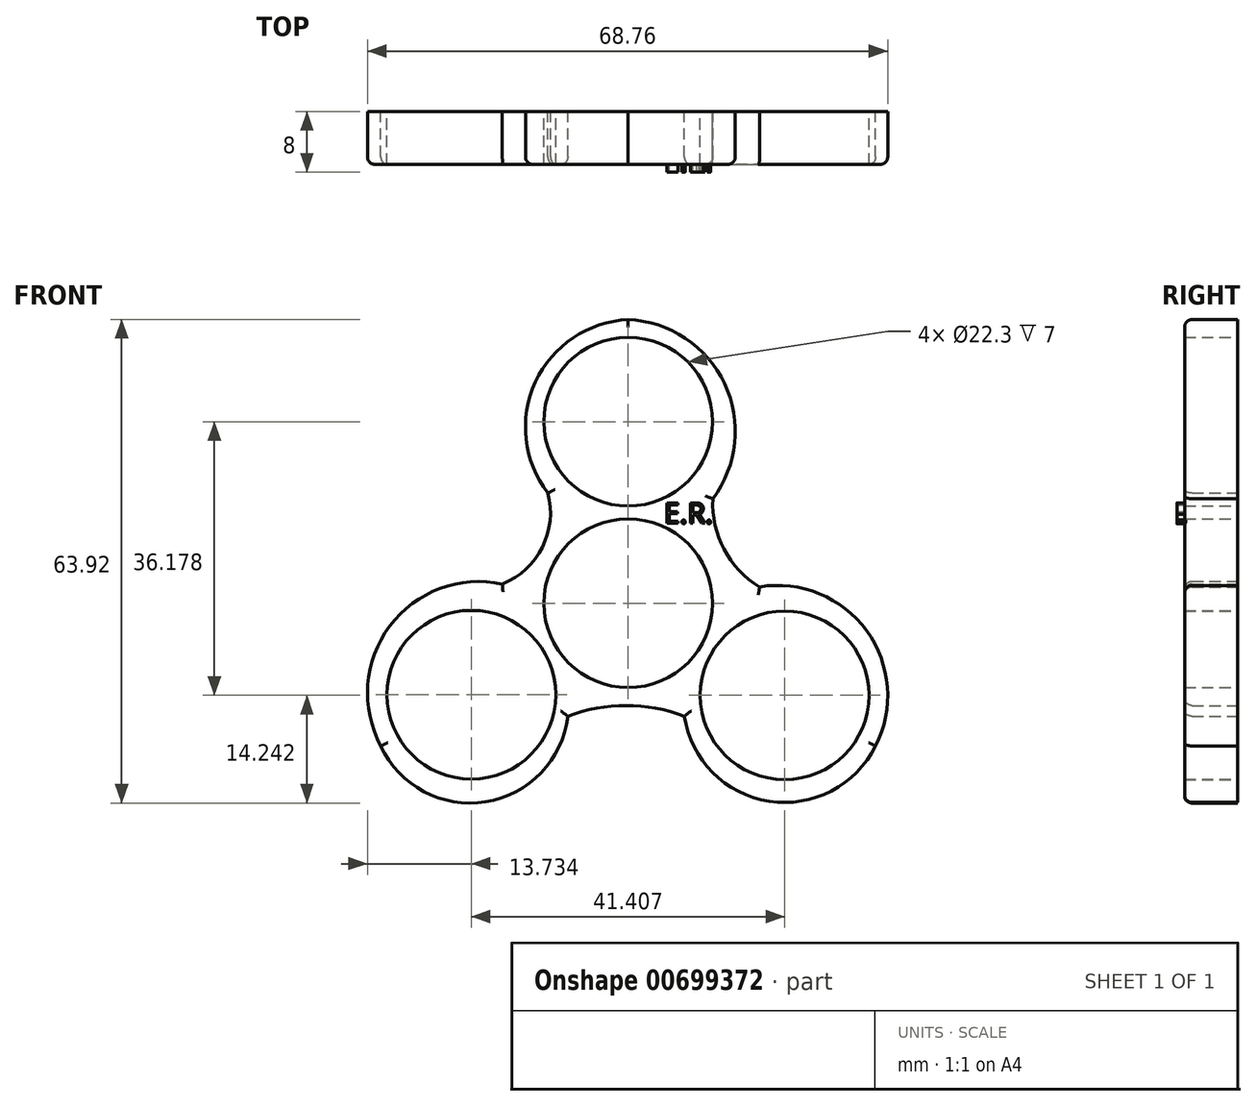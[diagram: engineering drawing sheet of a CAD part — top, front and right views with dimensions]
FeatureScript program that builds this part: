
annotation { "Feature Type Name" : "Feature", "Feature Type Description" : "" }
export const myFeature = defineFeature(function(context is Context, id is Id, definition is map)
    precondition{}
    {
        {
            var Q0;
            Q0=qCreatedBy(makeId("Front.planeOp"),FACE);
            var sketch = newSketch(context, id + "F0", { "sketchPlane" : qUnion([Q0])});
            skCircle(sketch, "E0", {"center": v(0, 0) * mm, "radius": 11.15 * mm});
            skCircle(sketch, "E1", {"center": v(0, 24) * mm, "radius": 11.15 * mm});
            skCircle(sketch, "E2", {"center": v(20.68, -12.18) * mm, "radius": 11.15 * mm});
            skCircle(sketch, "E3", {"center": v(-20.73, -12.1) * mm, "radius": 11.15 * mm});
            skLineSegment(sketch, "E4", {"start": v(0, 0) * mm, "end": v(-44.43, -25.65) * mm});
            skLineSegment(sketch, "E5", {"start": v(0, 0) * mm, "end": v(44.43, -25.65) * mm});
            skLineSegment(sketch, "E6", {"start": v(0, 0) * mm, "end": v(0, 54.97) * mm});
            skArc(sketch, "E7", {"start": v(-16.63, 2.54) * mm, "mid": v(-11.35, 7.41) * mm, "end": v(-10.62, 14.57) * mm});
            skArc(sketch, "E8", {"start": v(-16.63, 2.54) * mm, "mid": v(-31.51, -3.03) * mm, "end": v(-32.7, -18.88) * mm});
            skArc(sketch, "E9", {"start": v(-32.7, -18.88) * mm, "mid": v(-18.85, -26.26) * mm, "end": v(-7.99, -14.94) * mm});
            skArc(sketch, "E10", {"start": v(7.42, -14.94) * mm, "mid": v(-0.28, -13.53) * mm, "end": v(-7.99, -14.94) * mm});
            skArc(sketch, "E11", {"start": v(7.42, -14.94) * mm, "mid": v(18.62, -26.18) * mm, "end": v(32.7, -18.88) * mm});
            skArc(sketch, "E12", {"start": v(32.7, -18.88) * mm, "mid": v(31.51, -3.65) * mm, "end": v(17.39, 2.16) * mm});
            skArc(sketch, "E13", {"start": v(11.18, 13.81) * mm, "mid": v(12.67, 7.13) * mm, "end": v(17.39, 2.16) * mm});
            skArc(sketch, "E14", {"start": v(11.18, 13.81) * mm, "mid": v(12.74, 29.03) * mm, "end": v(0, 37.5) * mm});
            skArc(sketch, "E15", {"start": v(0, 37.5) * mm, "mid": v(-12.26, 29.25) * mm, "end": v(-10.62, 14.57) * mm});
            skSolve(sketch);
        }
        {
            var Q0;
            Q0 = qSketchRegion(id + "F0", true);
            extrude(context, id + "F1", {"entities" : qUnion([Q0]), "depth" : 7 * mm, "offsetDistance" : 25 * mm});
        }
        {
            var Q0;
            Q0=makeQuery(id+"F1.opExtrude","CAP_FACE",FACE,{"disambiguationData":[OSD([sQuery(id+"F0.wireOp",EDGE,"E0"),sQuery(id+"F0.wireOp",EDGE,"E1"),sQuery(id+"F0.wireOp",EDGE,"E2"),sQuery(id+"F0.wireOp",EDGE,"E3"),sQuery(id+"F0.wireOp",EDGE,"E7"),sQuery(id+"F0.wireOp",EDGE,"E8"),sQuery(id+"F0.wireOp",EDGE,"E9"),sQuery(id+"F0.wireOp",EDGE,"E10"),sQuery(id+"F0.wireOp",EDGE,"E11"),sQuery(id+"F0.wireOp",EDGE,"E12"),sQuery(id+"F0.wireOp",EDGE,"E13"),sQuery(id+"F0.wireOp",EDGE,"E14"),sQuery(id+"F0.wireOp",EDGE,"E15")])],"isStart":false});
            var sketch = newSketch(context, id + "F2", { "sketchPlane" : qUnion([Q0])});
            skText(sketch, "E16", { "text": "E.R.", "fontName": "OpenSans-Regular.ttf"});
            const initialGuessF2  = {"E16": [0.00472, 0.01055, 1, 0, 0.00273]};
            skSetInitialGuess(sketch, initialGuessF2);
            skSolve(sketch);
        }
        {
            var Q0;
            Q0 = qSketchRegion(id + "F2", true);
            extrude(context, id + "F3", {"entities" : qUnion([Q0]), "operationType" : NewBodyOperationType.ADD, "depth" : 1 * mm, "offsetDistance" : 25 * mm});
        }
        {
            var Q0;
            Q0=makeQuery(id+"F1.opExtrude","CAP_EDGE",EDGE,{"disambiguationData":[OSD([sQuery(id+"F0.wireOp",EDGE,"E7")])],"isStart":false});
            var Q1;
            Q1=makeQuery(id+"F1.opExtrude","CAP_EDGE",EDGE,{"disambiguationData":[OSD([sQuery(id+"F0.wireOp",EDGE,"E15")])],"isStart":false});
            var Q2;
            Q2=makeQuery(id+"F1.opExtrude","CAP_EDGE",EDGE,{"disambiguationData":[OSD([sQuery(id+"F0.wireOp",EDGE,"E14")])],"isStart":false});
            var Q3;
            Q3=makeQuery(id+"F1.opExtrude","CAP_EDGE",EDGE,{"disambiguationData":[OSD([sQuery(id+"F0.wireOp",EDGE,"E13")])],"isStart":false});
            var Q4;
            Q4=makeQuery(id+"F1.opExtrude","CAP_EDGE",EDGE,{"disambiguationData":[OSD([sQuery(id+"F0.wireOp",EDGE,"E12")])],"isStart":false});
            var Q5;
            Q5=makeQuery(id+"F1.opExtrude","CAP_EDGE",EDGE,{"disambiguationData":[OSD([sQuery(id+"F0.wireOp",EDGE,"E11")])],"isStart":false});
            var Q6;
            Q6=makeQuery(id+"F1.opExtrude","CAP_EDGE",EDGE,{"disambiguationData":[OSD([sQuery(id+"F0.wireOp",EDGE,"E10")])],"isStart":false});
            var Q7;
            Q7=makeQuery(id+"F1.opExtrude","CAP_EDGE",EDGE,{"disambiguationData":[OSD([sQuery(id+"F0.wireOp",EDGE,"E9")])],"isStart":false});
            var Q8;
            Q8=makeQuery(id+"F1.opExtrude","CAP_EDGE",EDGE,{"disambiguationData":[OSD([sQuery(id+"F0.wireOp",EDGE,"E8")])],"isStart":false});
            fillet(context, id + "F4", {"entities" : qUnion([Q0, Q1, Q2, Q3, Q4, Q5, Q6, Q7, Q8]), "radius" : 1 * mm, "tangentPropagation" : true, "allowEdgeOverflow" : false});
        }
    });
